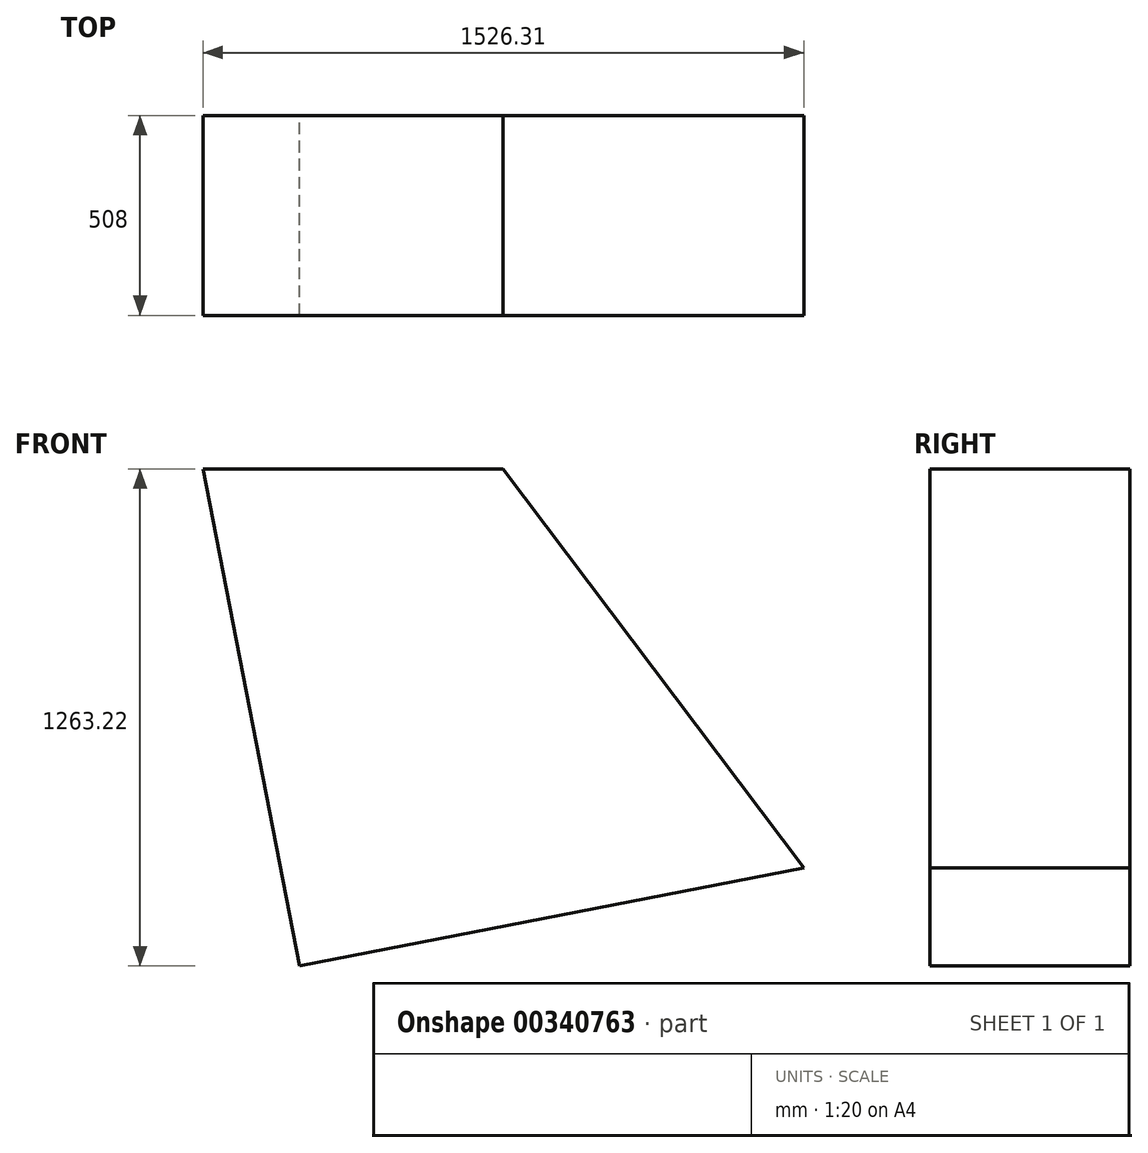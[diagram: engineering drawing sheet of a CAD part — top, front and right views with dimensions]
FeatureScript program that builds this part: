
annotation { "Feature Type Name" : "Feature", "Feature Type Description" : "" }
export const myFeature = defineFeature(function(context is Context, id is Id, definition is map)
    precondition{}
    {
        {
            var Q0;
            Q0=qCreatedBy(makeId("Front.planeOp"),FACE);
            var sketch = newSketch(context, id + "F0", { "sketchPlane" : qUnion([Q0])});
            skLineSegment(sketch, "E0", {"start": v(-762, 0) * mm, "end": v(0, 0) * mm});
            skLineSegment(sketch, "E1", {"start": v(0, 0) * mm, "end": v(764.3, -1014.27) * mm});
            skLineSegment(sketch, "E2", {"start": v(764.3, -1014.27) * mm, "end": v(-516.45, -1263.22) * mm});
            skLineSegment(sketch, "E3", {"start": v(-516.45, -1263.22) * mm, "end": v(-762, 0) * mm});
            skSolve(sketch);
        }
        {
            var Q0;
            Q0=makeQuery(id+"F0.imprint","IMPRINT",FACE,{"disambiguationData":[TD([[makeQuery(id+"F0.imprint","IMPRINT",EDGE,{"derivedFrom":sQuery(id+"F0.wireOp",EDGE,"E0")}),-1.0]])]});
            extrude(context, id + "F1", {"entities" : qUnion([Q0]), "depth" : 508 * mm});
        }
    });
